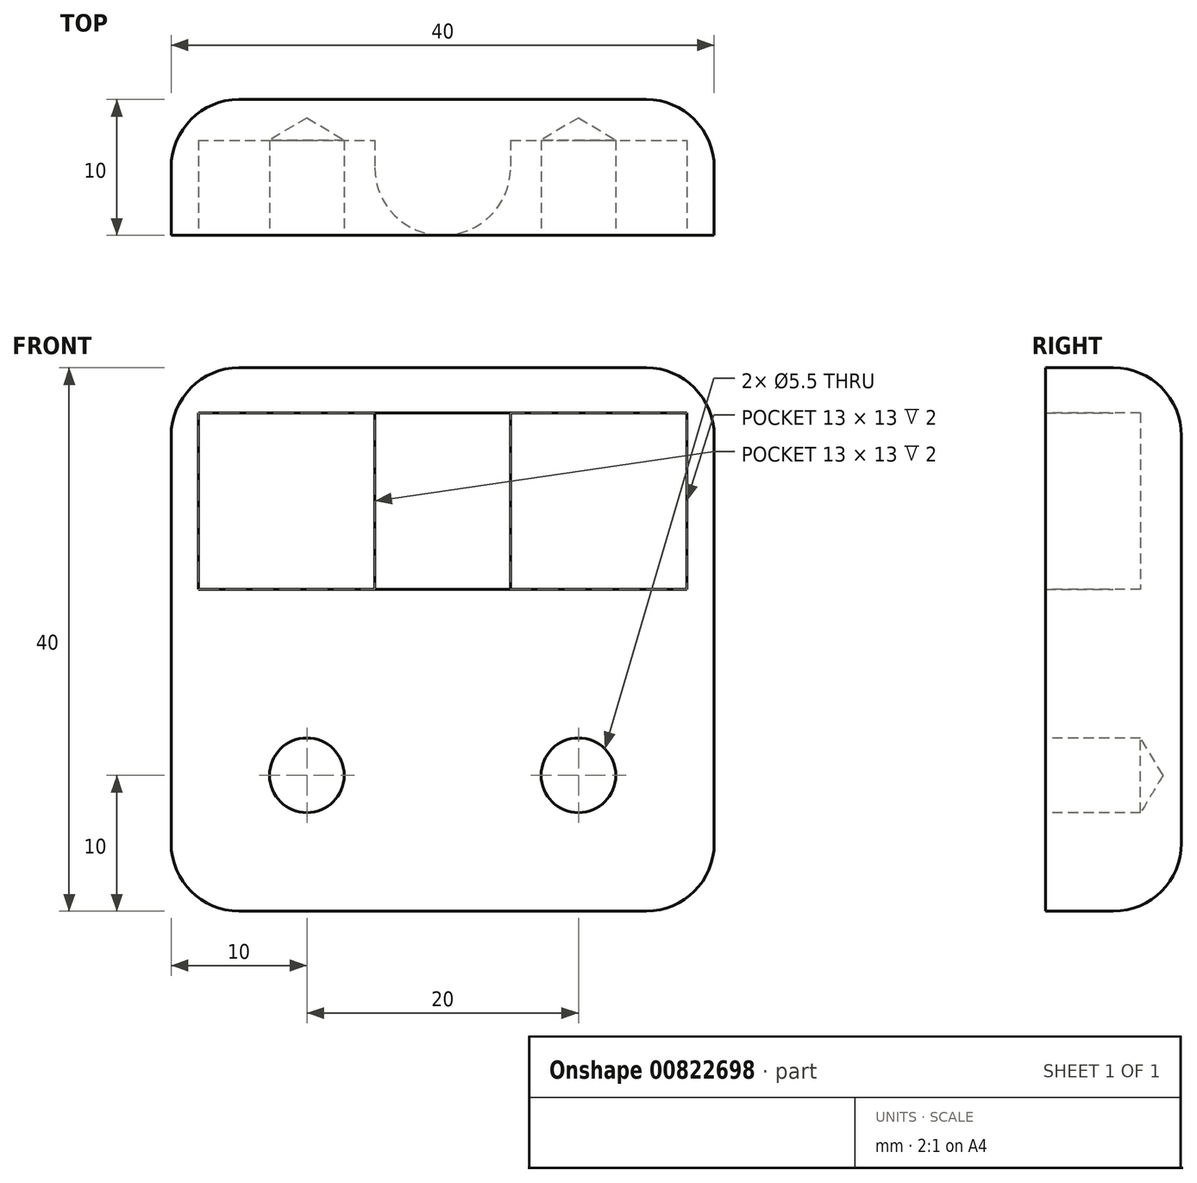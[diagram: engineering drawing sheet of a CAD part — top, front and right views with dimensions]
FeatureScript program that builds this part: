
annotation { "Feature Type Name" : "Feature", "Feature Type Description" : "" }
export const myFeature = defineFeature(function(context is Context, id is Id, definition is map)
    precondition{}
    {
        {
            var Q0;
            Q0=qCreatedBy(makeId("Front.planeOp"),FACE);
            var sketch = newSketch(context, id + "F0", { "sketchPlane" : qUnion([Q0])});
            skLineSegment(sketch, "E0.bottom", {"start": v(-20, 20) * mm, "end": v(20, 20) * mm});
            skLineSegment(sketch, "E0.top", {"start": v(-20, -20) * mm, "end": v(20, -20) * mm});
            skLineSegment(sketch, "E0.left", {"start": v(-20, 20) * mm, "end": v(-20, -20) * mm});
            skLineSegment(sketch, "E0.right", {"start": v(20, 20) * mm, "end": v(20, -20) * mm});
            skPoint(sketch, "E0.middle", {"position": v(0, 0) * mm});
            skLineSegment(sketch, "E1.bottom", {"start": v(-18, 16.69) * mm, "end": v(18, 16.69) * mm});
            skLineSegment(sketch, "E1.top", {"start": v(-18, 3.69) * mm, "end": v(18, 3.69) * mm});
            skLineSegment(sketch, "E1.left", {"start": v(-18, 16.69) * mm, "end": v(-18, 3.69) * mm});
            skLineSegment(sketch, "E1.right", {"start": v(18, 16.69) * mm, "end": v(18, 3.69) * mm});
            skPoint(sketch, "E1.middle", {"position": v(0, 10.19) * mm});
            skLineSegment(sketch, "E2.bottom", {"start": v(-5, 16.69) * mm, "end": v(5, 16.69) * mm});
            skLineSegment(sketch, "E2.top", {"start": v(-5, 3.69) * mm, "end": v(5, 3.69) * mm});
            skLineSegment(sketch, "E2.left", {"start": v(-5, 16.69) * mm, "end": v(-5, 3.69) * mm});
            skLineSegment(sketch, "E2.right", {"start": v(5, 16.69) * mm, "end": v(5, 3.69) * mm});
            skPoint(sketch, "E3", {"position": v(-10, -10) * mm});
            skPoint(sketch, "E4", {"position": v(10, -10) * mm});
            skSolve(sketch);
        }
        {
            var Q0;
            Q0=makeQuery(id+"F0.imprint","IMPRINT",FACE,{"disambiguationData":[TD([[makeQuery(id+"F0.imprint","IMPRINT",EDGE,{"derivedFrom":sQuery(id+"F0.wireOp",EDGE,"E0.bottom")}),-1.0]])]});
            var Q1;
            {var subQ0=sQuery(id+"F0.wireOp",EDGE,"FkQTs3SL-2HNJ-xTWw-svT9-O1Nr5TyXCMKe");var subQ3=sQuery(id+"F0.wireOp",EDGE,"Dvc2s5Ip-L40u-J8UN-cv7M-KRq48KJUc47l");var subQ4=makeQuery(id+"F0.imprint","INTERSECT",VERTEX,{"disambiguationData":[OD(0.0)],"derivedFrom":[subQ0,subQ3]});Q1=makeQuery(id+"F0.imprint","IMPRINT",FACE,{"disambiguationData":[TD([[makeQuery(id+"F0.imprint","IMPRINT",EDGE,{"disambiguationData":[TD([[subQ4,-1.0]])],"derivedFrom":subQ3}),-1.0]])]});}
            var Q2;
            {var subQ0=sQuery(id+"F0.wireOp",EDGE,"D4uOrA4J-H9wG-Jy52-jYg1-4lKW49JMURe3");var subQ3=sQuery(id+"F0.wireOp",EDGE,"DxL6IU4n-wEOo-3Iyj-lIlw-wuwWEbap7Sak");var subQ4=makeQuery(id+"F0.imprint","INTERSECT",VERTEX,{"disambiguationData":[OD(0.0)],"derivedFrom":[subQ0,subQ3]});Q2=makeQuery(id+"F0.imprint","IMPRINT",FACE,{"disambiguationData":[TD([[makeQuery(id+"F0.imprint","IMPRINT",EDGE,{"disambiguationData":[TD([[subQ4,-1.0]])],"derivedFrom":subQ3}),-1.0]])]});}
            var Q3;
            {var subQ7=sQuery(id+"F0.wireOp",EDGE,"KzlJazcu-56S6-VWu3-KPi9-e0OXTOBnhC3g");Q3=makeQuery(id+"F0.imprint","IMPRINT",FACE,{"disambiguationData":[TD([[makeQuery(id+"F0.imprint","IMPRINT",EDGE,{"derivedFrom":subQ7}),-1.0]])]});}
            var Q4;
            {var subQ0=sQuery(id+"F0.wireOp",EDGE,"Dvc2s5Ip-L40u-J8UN-cv7M-KRq48KJUc47l");var subQ1=sQuery(id+"F0.wireOp",EDGE,"FkQTs3SL-2HNJ-xTWw-svT9-O1Nr5TyXCMKe");var subQ2=makeQuery(id+"F0.imprint","INTERSECT",VERTEX,{"disambiguationData":[OD(0.0)],"derivedFrom":[subQ1,subQ0]});Q4=makeQuery(id+"F0.imprint","IMPRINT",FACE,{"disambiguationData":[TD([[makeQuery(id+"F0.imprint","IMPRINT",EDGE,{"disambiguationData":[TD([[subQ2,-1.0]])],"derivedFrom":subQ1}),-1.0]])]});}
            var Q5;
            {var subQ0=sQuery(id+"F0.wireOp",EDGE,"Dvc2s5Ip-L40u-J8UN-cv7M-KRq48KJUc47l");var subQ1=sQuery(id+"F0.wireOp",EDGE,"FkQTs3SL-2HNJ-xTWw-svT9-O1Nr5TyXCMKe");var subQ2=makeQuery(id+"F0.imprint","INTERSECT",VERTEX,{"disambiguationData":[OD(0.0)],"derivedFrom":[subQ1,subQ0]});Q5=makeQuery(id+"F0.imprint","IMPRINT",FACE,{"disambiguationData":[TD([[makeQuery(id+"F0.imprint","IMPRINT",EDGE,{"disambiguationData":[TD([[subQ2,-1.0]])],"derivedFrom":subQ1}),1.0]])]});}
            var Q6;
            {var subQ0=sQuery(id+"F0.wireOp",EDGE,"DxL6IU4n-wEOo-3Iyj-lIlw-wuwWEbap7Sak");var subQ1=sQuery(id+"F0.wireOp",EDGE,"D4uOrA4J-H9wG-Jy52-jYg1-4lKW49JMURe3");var subQ2=makeQuery(id+"F0.imprint","INTERSECT",VERTEX,{"disambiguationData":[OD(0.0)],"derivedFrom":[subQ1,subQ0]});Q6=makeQuery(id+"F0.imprint","IMPRINT",FACE,{"disambiguationData":[TD([[makeQuery(id+"F0.imprint","IMPRINT",EDGE,{"disambiguationData":[TD([[subQ2,-1.0]])],"derivedFrom":subQ1}),-1.0]])]});}
            var Q7;
            {var subQ0=sQuery(id+"F0.wireOp",EDGE,"DxL6IU4n-wEOo-3Iyj-lIlw-wuwWEbap7Sak");var subQ1=sQuery(id+"F0.wireOp",EDGE,"D4uOrA4J-H9wG-Jy52-jYg1-4lKW49JMURe3");var subQ2=makeQuery(id+"F0.imprint","INTERSECT",VERTEX,{"disambiguationData":[OD(0.0)],"derivedFrom":[subQ1,subQ0]});Q7=makeQuery(id+"F0.imprint","IMPRINT",FACE,{"disambiguationData":[TD([[makeQuery(id+"F0.imprint","IMPRINT",EDGE,{"disambiguationData":[TD([[subQ2,-1.0]])],"derivedFrom":subQ1}),1.0]])]});}
            var Q8;
            {var subQ2=sQuery(id+"F0.wireOp",EDGE,"E1.right");var subQ4=sQuery(id+"F0.wireOp",EDGE,"E1.left");Q8=qUnion([makeQuery(id+"F0.imprint","IMPRINT",FACE,{"disambiguationData":[TD([[makeQuery(id+"F0.imprint","IMPRINT",EDGE,{"derivedFrom":subQ4}),1.0]])]}),makeQuery(id+"F0.imprint","IMPRINT",FACE,{"disambiguationData":[TD([[makeQuery(id+"F0.imprint","IMPRINT",EDGE,{"derivedFrom":subQ2}),-1.0]])]})]);}
            extrude(context, id + "F1", {"entities" : qUnion([Q0, Q1, Q2, Q3, Q4, Q5, Q6, Q7, Q8]), "oppositeDirection" : true, "depth" : 10 * mm, "offsetDistance" : 25 * mm});
        }
        {
            var Q0;
            {var subQ2=sQuery(id+"F0.wireOp",EDGE,"E1.right");var subQ4=sQuery(id+"F0.wireOp",EDGE,"E1.left");Q0=qUnion([makeQuery(id+"F0.imprint","IMPRINT",FACE,{"disambiguationData":[TD([[makeQuery(id+"F0.imprint","IMPRINT",EDGE,{"derivedFrom":subQ4}),1.0]])]}),makeQuery(id+"F0.imprint","IMPRINT",FACE,{"disambiguationData":[TD([[makeQuery(id+"F0.imprint","IMPRINT",EDGE,{"derivedFrom":subQ2}),-1.0]])]})]);}
            var Q1;
            {var subQ0=sQuery(id+"F0.wireOp",EDGE,"DxL6IU4n-wEOo-3Iyj-lIlw-wuwWEbap7Sak");var subQ1=sQuery(id+"F0.wireOp",EDGE,"D4uOrA4J-H9wG-Jy52-jYg1-4lKW49JMURe3");var subQ2=makeQuery(id+"F0.imprint","INTERSECT",VERTEX,{"disambiguationData":[OD(0.0)],"derivedFrom":[subQ1,subQ0]});Q1=makeQuery(id+"F0.imprint","IMPRINT",FACE,{"disambiguationData":[TD([[makeQuery(id+"F0.imprint","IMPRINT",EDGE,{"disambiguationData":[TD([[subQ2,-1.0]])],"derivedFrom":subQ1}),1.0]])]});}
            var Q2;
            {var subQ0=sQuery(id+"F0.wireOp",EDGE,"DxL6IU4n-wEOo-3Iyj-lIlw-wuwWEbap7Sak");var subQ1=sQuery(id+"F0.wireOp",EDGE,"D4uOrA4J-H9wG-Jy52-jYg1-4lKW49JMURe3");var subQ2=makeQuery(id+"F0.imprint","INTERSECT",VERTEX,{"disambiguationData":[OD(0.0)],"derivedFrom":[subQ1,subQ0]});Q2=makeQuery(id+"F0.imprint","IMPRINT",FACE,{"disambiguationData":[TD([[makeQuery(id+"F0.imprint","IMPRINT",EDGE,{"disambiguationData":[TD([[subQ2,-1.0]])],"derivedFrom":subQ1}),-1.0]])]});}
            var Q3;
            {var subQ0=sQuery(id+"F0.wireOp",EDGE,"Dvc2s5Ip-L40u-J8UN-cv7M-KRq48KJUc47l");var subQ1=sQuery(id+"F0.wireOp",EDGE,"FkQTs3SL-2HNJ-xTWw-svT9-O1Nr5TyXCMKe");var subQ2=makeQuery(id+"F0.imprint","INTERSECT",VERTEX,{"disambiguationData":[OD(0.0)],"derivedFrom":[subQ1,subQ0]});Q3=makeQuery(id+"F0.imprint","IMPRINT",FACE,{"disambiguationData":[TD([[makeQuery(id+"F0.imprint","IMPRINT",EDGE,{"disambiguationData":[TD([[subQ2,-1.0]])],"derivedFrom":subQ1}),-1.0]])]});}
            var Q4;
            {var subQ0=sQuery(id+"F0.wireOp",EDGE,"Dvc2s5Ip-L40u-J8UN-cv7M-KRq48KJUc47l");var subQ1=sQuery(id+"F0.wireOp",EDGE,"FkQTs3SL-2HNJ-xTWw-svT9-O1Nr5TyXCMKe");var subQ2=makeQuery(id+"F0.imprint","INTERSECT",VERTEX,{"disambiguationData":[OD(0.0)],"derivedFrom":[subQ1,subQ0]});Q4=makeQuery(id+"F0.imprint","IMPRINT",FACE,{"disambiguationData":[TD([[makeQuery(id+"F0.imprint","IMPRINT",EDGE,{"disambiguationData":[TD([[subQ2,-1.0]])],"derivedFrom":subQ1}),1.0]])]});}
            extrude(context, id + "F2", {"entities" : qUnion([Q0, Q1, Q2, Q3, Q4]), "operationType" : NewBodyOperationType.REMOVE, "oppositeDirection" : true, "depth" : 7 * mm, "offsetDistance" : 25 * mm});
        }
        {
            var Q0;
            {var subQ2=sQuery(id+"F0.wireOp",EDGE,"E2.left");Q0=makeQuery(id+"F0.imprint","IMPRINT",FACE,{"disambiguationData":[TD([[makeQuery(id+"F0.imprint","IMPRINT",EDGE,{"derivedFrom":subQ2}),1.0]])]});}
            extrude(context, id + "F3", {"entities" : qUnion([Q0]), "operationType" : NewBodyOperationType.ADD, "oppositeDirection" : true, "depth" : 10 * mm, "offsetDistance" : 25 * mm});
        }
        {
            var Q0;
            Q0=makeQuery(id+"F3.opExtrude","CAP_EDGE",EDGE,{"disambiguationData":[OSD([sQuery(id+"F0.wireOp",EDGE,"E2.right")])],"isStart":true});
            var Q1;
            Q1=makeQuery(id+"F3.opExtrude","CAP_EDGE",EDGE,{"disambiguationData":[OSD([sQuery(id+"F0.wireOp",EDGE,"E2.left")])],"isStart":true});
            fillet(context, id + "F4", {"entities" : qUnion([Q0, Q1]), "radius" : 5 * mm, "tangentPropagation" : true, "allowEdgeOverflow" : false});
        }
        {
            var Q0;
            Q0=makeQuery(id+"F1.opExtrude","CAP_EDGE",EDGE,{"disambiguationData":[OSD([sQuery(id+"F0.wireOp",EDGE,"E0.bottom")])],"isStart":false});
            var Q1;
            Q1=makeQuery(id+"F1.opExtrude","SWEPT_EDGE",EDGE,{"disambiguationData":[OSD([sQuery(id+"F0.wireOp",EDGE,"E0.bottom"),sQuery(id+"F0.wireOp",EDGE,"E0.right")])]});
            var Q2;
            Q2=makeQuery(id+"F1.opExtrude","SWEPT_EDGE",EDGE,{"disambiguationData":[OSD([sQuery(id+"F0.wireOp",EDGE,"E0.bottom"),sQuery(id+"F0.wireOp",EDGE,"E0.left")])]});
            var Q3;
            Q3=makeQuery(id+"F1.opExtrude","SWEPT_EDGE",EDGE,{"disambiguationData":[OSD([sQuery(id+"F0.wireOp",EDGE,"E0.top"),sQuery(id+"F0.wireOp",EDGE,"E0.right")])]});
            var Q4;
            Q4=makeQuery(id+"F1.opExtrude","CAP_EDGE",EDGE,{"disambiguationData":[OSD([sQuery(id+"F0.wireOp",EDGE,"E0.top")])],"isStart":false});
            var Q5;
            Q5=makeQuery(id+"F1.opExtrude","SWEPT_EDGE",EDGE,{"disambiguationData":[OSD([sQuery(id+"F0.wireOp",EDGE,"E0.top"),sQuery(id+"F0.wireOp",EDGE,"E0.left")])]});
            var Q6;
            {var subQ0=sQuery(id+"F0.wireOp",EDGE,"E2.right");var subQ1=sQuery(id+"F0.wireOp",EDGE,"E2.left");var subQ2=sQuery(id+"F0.wireOp",EDGE,"E1.top");var subQ3=sQuery(id+"F0.wireOp",EDGE,"E1.bottom");Q6=makeQuery(id+"F3.boolean.opBoolean","MERGE",FACE,{"derivedFrom":[makeQuery(id+"F1.opExtrude","CAP_FACE",FACE,{"disambiguationData":[OSD([sQuery(id+"F0.wireOp",EDGE,"E0.bottom"),sQuery(id+"F0.wireOp",EDGE,"E0.top"),sQuery(id+"F0.wireOp",EDGE,"E0.left"),sQuery(id+"F0.wireOp",EDGE,"E0.right"),subQ3,subQ2,subQ1,subQ0])],"isStart":false}),makeQuery(id+"F3.opExtrude","CAP_FACE",FACE,{"disambiguationData":[OSD([subQ3,subQ2,subQ1,subQ0])],"isStart":false})]});}
            fillet(context, id + "F5", {"entities" : qUnion([Q0, Q1, Q2, Q3, Q4, Q5, Q6]), "radius" : 5 * mm, "tangentPropagation" : true, "allowEdgeOverflow" : false});
        }
        {
            var Q0;
            Q0=sQuery(id+"F0.wireOp",VERTEX,"E3");
            var Q1;
            Q1=sQuery(id+"F0.wireOp",VERTEX,"E4");
            var Q2;
            Q2=makeQuery(id+"F1.opExtrude","SWEPT_BODY",BODY,{"disambiguationData":[OSD([sQuery(id+"F0.wireOp",EDGE,"E0.bottom"),sQuery(id+"F0.wireOp",EDGE,"E0.top"),sQuery(id+"F0.wireOp",EDGE,"E0.left"),sQuery(id+"F0.wireOp",EDGE,"E0.right"),sQuery(id+"F0.wireOp",EDGE,"E1.bottom"),sQuery(id+"F0.wireOp",EDGE,"E1.top"),sQuery(id+"F0.wireOp",EDGE,"E2.left"),sQuery(id+"F0.wireOp",EDGE,"E2.right")])]});
            hole(context, id + "F6", {"style" : HoleStyle.SIMPLE, "endStyle" : HoleEndStyle.BLIND, "standardTappedOrClearance" : lookupTablePath({ "fit" : "Normal", "standard" : "ISO", "size" : "M5", "type" : "Clearance" }), "standardBlindInLast" : lookupTablePath({ "fit" : "Standard", "standard" : "ISO", "size" : "M5", "type" : "Clearance" }), "holeDiameter" : 5.5 * mm, "majorDiameter" : 5 * mm, "holeDepth" : 7 * mm, "isTappedThrough" : true, "tappedDepth" : 12 * mm, "tapClearance" : 3, "locations" : qUnion([Q0, Q1]), "scope" : qUnion([Q2])});
        }
    });
